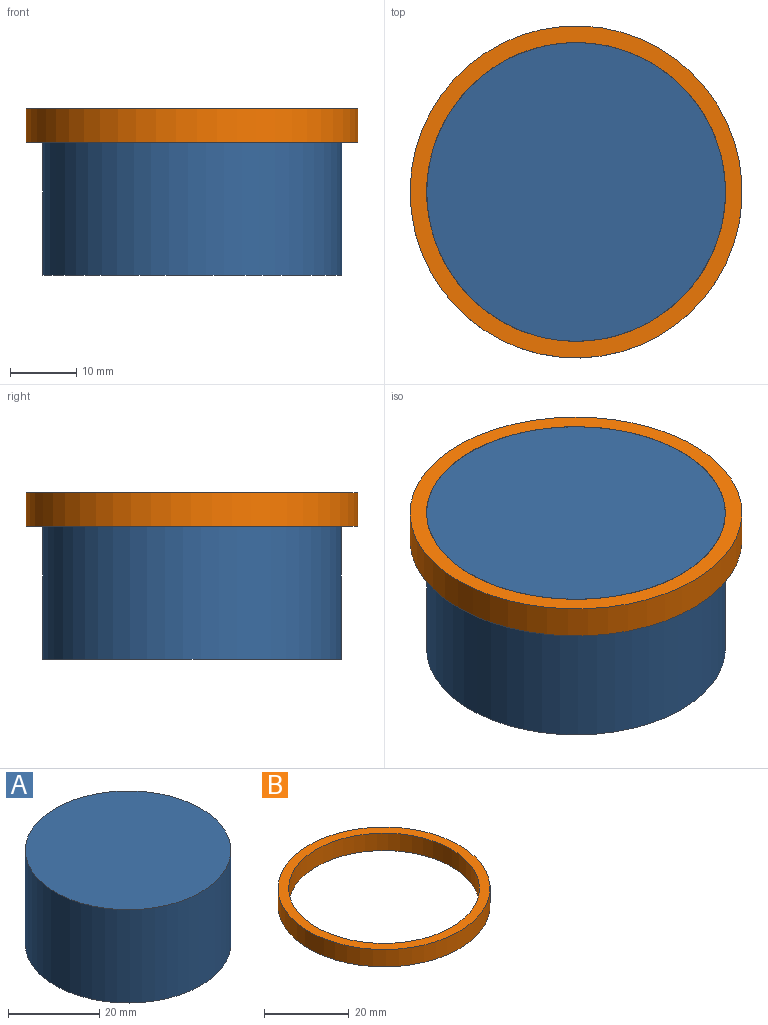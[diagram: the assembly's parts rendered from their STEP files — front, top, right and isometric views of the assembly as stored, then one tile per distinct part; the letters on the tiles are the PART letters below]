
ASSEMBLY  parts=2 mates=1
PART A: 3 faces, bbox 45x45x25 mm
  f0: cylinder r=22.5mm len=45mm, axis (0,0,-1), area 3534.3mm2, adj f1,f2
  f1: plane 45x45mm, normal (0,0,1), area 1590.4mm2, adj f0
  f2: plane 45x45mm, normal (0,0,-1), area 1590.4mm2, adj f0
PART B: 4 faces, bbox 50x50x5 mm
  f0: cylinder r=22.5mm len=45mm, axis (0,0,-1), area 706.9mm2, adj f2,f3
  f1: cylinder r=25mm len=50mm, axis (0,0,-1), area 785.4mm2, adj f2,f3
  f2: plane 50x50mm, normal (0,0,1), area 373.1mm2, adj f0,f1
  f3: plane 50x50mm, normal (0,0,-1), area 373.1mm2, adj f0,f1
PLACE A t=(27.86,10.72,-8.05)mm fixed
PLACE B rot(axis=(0,0,1),88deg) t=(27.86,10.72,11.95)mm
MATE revolute B.f0 <-> A.f0  axis (0,0,1) through (27.86,10.72,16.95)mm
